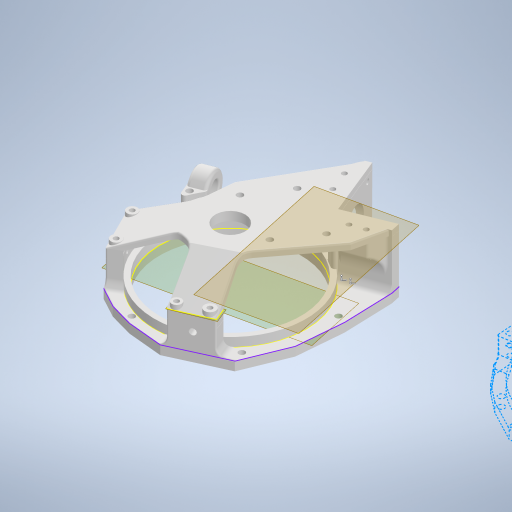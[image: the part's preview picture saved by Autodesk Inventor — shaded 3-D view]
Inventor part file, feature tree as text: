
AUTODESK INVENTOR PART (.ipt)
format: ipt  version: 2023.1 (Build 271208000, 208)  size: 1,651,712 bytes
history: native  units: in
note: dims shown in document units (in); Inventor stores cm internally (conversion verified against a paired STEP export)
features: sketch x21, extrude x20, fillet x17, other x11, hole x6, plane x5, projected_geometry x3, loft x2, split x1
ambient origin geometry x8: Origin, YZ Plane, XZ Plane, XY Plane, X Axis, Y Axis, Z Axis, Center Point
bodies: Solid1 (feature_tree), Solid4 (feature_tree), Solid5 (feature_tree)
feature tree (86):
  plane  "Work Plane1"
  sketch  "Sketch1"  dims[d0=0.1575in d1=0.0in d2=0.2402in d3=0.2362in d4=0.0in d5=0.0in]
  plane  "Work Plane2"
  sketch  "Sketch2"  dims[d6=0.2362in d7=0.0787in]
  extrude  "Extrusion1"  Depth=0.2402in TaperAngle=0.0deg
  extrude  "Extrusion2"  Depth=0.0787in
  fillet  "Fillet1"  Radius=1.375in
  fillet  "Fillet2"  Radius=0.7874in
  sketch  "Sketch3"  dims[d13=0.1575in d14=0.0719in d15=0.0in d16=0.0in]
  extrude  "Extrusion4"  Depth=0.0787in TaperAngle=0.0deg
  extrude  "Extrusion5"  Depth=0.8681in TaperAngle=0.0deg
  plane  "Work Plane3"
  sketch  "Sketch5"  dims[d17=0.1575in d18=1.6014in d19=0.0in d20=0.0in d23=1.375in d24=0.7874in]
  extrude  "Extrusion7"  Depth=0.8681in TaperAngle=0.0deg
  extrude  "Extrusion8"  Depth=0.0787in
  extrude  "Extrusion9"  Depth=0.1969in
  extrude  "Extrusion12"  TaperAngle=0.0deg  [1 undecoded]
  sketch  "Sketch8"  dims[d25=0.1575in d26=0.0in d27=0.0787in d28=0.2362in d29=0.0in d30=0.0in]
  plane  "Work Plane6"
  extrude  "Extrusion13"  TaperAngle=0.0deg  [1 undecoded]
  extrude  "Extrusion14"  Depth=0.3937in
  fillet  "Fillet4"  Radius=0.1969in
  fillet  "Fillet5"  Radius=0.0394in
  fillet  "Fillet6"  Radius=0.3937in
  fillet  "Fillet13"  Radius=0.3937in
  fillet  "Fillet15"  Radius=0.5906in
  loft  "Loft1"
  loft  "Loft2"
  fillet  "Fillet16"  Radius=0.1339in
  fillet  "Fillet17"  Radius=0.1339in
  fillet  "Fillet18"  Radius=0.1339in
  extrude  "Extrusion17"  Depth=1.5586in TaperAngle=0.0deg
  extrude  "Extrusion18"  Depth=0.0394in
  fillet  "Fillet21"  Radius=0.0394in
  extrude  "Extrusion19"  Depth=0.0394in TaperAngle=0.0deg
  fillet  "Fillet22"  Radius=0.0787in
  hole  "Hole1"  [1 undecoded]
  extrude  "Extrusion20"  Depth=0.3937in
  sketch  "Sketch19"  dims[d67=0.1969in d68=0.0in d69=90.0deg]
  extrude  "Extrusion21"  Depth=0.3937in
  extrude  "Extrusion22"  Depth=0.3937in
  fillet  "Fillet23"  Radius=0.1654in
  fillet  "Fillet24"  Radius=0.2756in
  fillet  "Fillet25"  Radius=0.1654in
  extrude  "Extrusion23"  Depth=0.3937in
  fillet  "Fillet26"  Radius=0.1654in
  fillet  "Fillet27"  Radius=0.1654in
  hole  "Hole2"  [1 undecoded]
  hole  "Hole3"  [1 undecoded]
  hole  "Hole4"  [1 undecoded]
  hole  "Hole5"  [1 undecoded]
  hole  "Hole6"  [1 undecoded]
  plane  "Work Plane8"
  extrude  "Extrusion24"  [1 undecoded]
  split  "Split2"
  extrude  "Extrusion25"  [1 undecoded]
  extrude  "Extrusion26"  [1 undecoded]
  projected_geometry  "Projected Loop1"
  projected_geometry  "Projected Loop2"
  projected_geometry  "Projected Loop4"
  other  "Edges1"
  other  "Edges2"
  other  "Edges3"
  other  "Edges4"
  sketch  "Sketch15"  dims[d31=0.2402in d32=0.0039in d33=0.0in d34=0.0in d41=0.8681in d42=0.0in]
  sketch  "Sketch16"  dims[d47=0.7805in d48=0.0in d49=0.8681in d50=0.0in]
  sketch  "Sketch17"  dims[d53=0.0787in d54=0.0787in]
  sketch  "Sketch18"  dims[d55=0.0787in d65=0.1969in]
  sketch  "Sketch20"  dims[d70=0.0in d71=90.0deg d72=0.0in d73=90.0deg]
  sketch  "Sketch22"  dims[d74=0.0in d75=90.0deg d76=0.3937in d77=0.1969in d78=0.0394in d81=0.3937in d82=0.0in d83=0.3937in d84=0.0in d85=0.5906in]
  sketch  "Sketch23"  dims[d86=0.3937in d87=0.0in d88=0.5906in]
  sketch  "Sketch24"  dims[d89=0.1339in d90=0.2362in d91=0.1575in d92=0.0787in d93=90.0deg d94=0.3937in d95=0.0in d96=0.1339in d97=0.1339in d98=0.1339in d99=0.1339in]
  sketch  "Sketch25"  dims[d100=1.4961in d101=0.0in d102=1.5586in d103=0.0in]
  sketch  "Sketch26"  dims[d104=0.4315in d105=0.0in d106=0.0787in d107=0.0394in]
  sketch  "Sketch27"  dims[d108=0.0394in d109=0.7805in d110=0.0in d111=0.0787in]
  sketch  "Sketch28"  dims[d112=0.1969in]
  sketch  "Sketch29"  dims[d113=0.1654in d114=0.2362in d115=0.1575in d116=0.0787in d117=90.0deg d118=0.3937in d119=0.0in]
  sketch  "Sketch30"  dims[d120=0.1654in d121=0.2362in d122=0.1575in d123=0.0787in d124=90.0deg d125=0.3937in d126=0.0in]
  sketch  "Sketch31"  dims[d127=0.1654in d128=0.2362in d129=0.1575in d130=0.0787in d131=90.0deg d132=0.3937in d133=0.0in d134=0.1654in d135=0.2362in d136=0.1575in d137=0.0787in d138=90.0deg d139=0.3937in d140=0.0in d141=0.1654in d142=0.2362in d143=0.1575in d144=0.0787in d145=90.0deg d146=0.3937in d147=0.0in d148=0.122in d149=0.0in d150=0.1654in d151=0.1654in d152=0.1654in d153=0.1654in d154=0.2756in d155=0.0in d156=0.1654in d157=0.1654in d158=0.1654in d159=0.1654in d160=0.2756in d161=0.0in d79=0.0in d80=0.0in]
  other  "G:\Assembly1.iam"
  other  "Assembly1.iam"
  other  "Nema 17 Stepper Motor:1"
  other  "Nema 17 Top Cap:1"
  other  "Part48:1"
  other  "Worm Gears:1"
  other  "Worm:1"
note: 11 required parameter values undecoded (feature->parameter linkage not recoverable at this tier; creation-order binding heuristic only, values carry confidence <= 0.55)
